# Revit family: Heater-QMark-Explosion_Proof_Convection_Heater_Gen2
name_source: partatom
category: Mechanical Equipment
units: mm (PartAtom-declared; Revit-internal decimal feet)

## family parameters
Classification = None
Cut with Voids When Loaded = No
Host = Face
OmniClass Number = 23.75.70.17.14
OmniClass Title = Convectors
Part Type = Normal
Room Calculation Point = No
Round Connector Dimension = Use Diameter
Shared = No

## types (191) — shared parameters
Default Elevation = 3' - 0"
Description = Electric explosion proof convection heater
Instruction Sheet Link = https://www.marleymep.com
Manufacturer = Marley® Engineered Products
Material = Paint - Berko - Tan
Number of Poles = 1
Product Documentation Link = https://www.marleymep.com
Product Name = Explosion - Proof Convection Heater Gen2
Product Page URL = https://www.marleymep.com
URL = https://www.marleymep.com
Version = 2020 - v1.0a

## per-type parameters (varying)
| type | Amps | Classification | Controls Only | Depth | Frequency | Height | Length | Phase | Power Factor | S1 - L 26in | S2 - L 26in | S2 - L 39in | S2 - L 67.5in | Shipping Weight | Thermostat only or w/controls | Total Heating Capacity | Unit Size | Voltage | Watts |
| Not a Type - Load Type Catalog | 0 A | Class I- Divisions 1 & 2- Groups B- C & D / Class I- Zones 1 & 2 Groups IIB + H2 / Ignition Temperature Code T2A- 536° F |  | 0' - 4 1/2" | 0 Hz | 0' - 6" | 2' - 2" | 1 | 0 | Yes | No | No | No |  |  | 0.0 Btu/h | 0 | 0 V | 0 W |
| QX-254-F0310052B | 4 A | Class I- Divisions 1 & 2- Groups B- C & D / Class I- Zones 1 & 2 Groups IIB + H2 / Ignition Temperature Code T2A- 536° F |  | 0' - 4 1/2" | 60 Hz | 0' - 6" | 2' - 2" | 1 | 1 | Yes | No | No | No | 13 lbs | 1024754 | 1706.0 Btu/h | 1 | 120 V | 500 W |
| QX-254-F0310052C | 2 A | Class I- Divisions 1 & 2- Groups B- C & D / Class I- Zones 1 & 2 Groups IIB + H2 / Ignition Temperature Code T2A- 536° F |  | 0' - 4 1/2" | 60 Hz | 0' - 6" | 2' - 2" | 1 | 1 | Yes | No | No | No | 13 lbs | 1024754 | 1706.0 Btu/h | 1 | 208 V | 500 W |
| QX-254-F0310052J | 2 A | Class I- Divisions 1 & 2- Groups B- C & D / Class I- Zones 1 & 2 Groups IIB + H2 / Ignition Temperature Code T2A- 536° F |  | 0' - 4 1/2" | 60 Hz | 0' - 6" | 2' - 2" | 1 | 1 | Yes | No | No | No | 13 lbs | 1024754 | 1706.0 Btu/h | 1 | 240 V | 500 W |
| QX-254-F0310052N | 2 A | Class I- Divisions 1 & 2- Groups B- C & D / Class I- Zones 1 & 2 Groups IIB + H2 / Ignition Temperature Code T2A- 536° F |  | 0' - 4 1/2" | 60 Hz | 0' - 6" | 2' - 2" | 1 | 1 | Yes | No | No | No | 13 lbs | 1024754 | 1706.0 Btu/h | 1 | 277 V | 500 W |
| QX-254-F0310102B | 8 A | Class I- Divisions 1 & 2- Groups B- C & D / Class I- Zones 1 & 2 Groups IIB + H2 / Ignition Temperature Code T2A- 536° F |  | 0' - 4 1/2" | 60 Hz | 0' - 6" | 2' - 2" | 1 | 1 | Yes | No | No | No | 13 lbs | 1024754 | 3412.0 Btu/h | 1 | 120 V | 1000 W |
| QX-254-F0310102C | 5 A | Class I- Divisions 1 & 2- Groups B- C & D / Class I- Zones 1 & 2 Groups IIB + H2 / Ignition Temperature Code T2A- 536° F |  | 0' - 4 1/2" | 60 Hz | 0' - 6" | 2' - 2" | 1 | 1 | Yes | No | No | No | 13 lbs | 1024754 | 3412.0 Btu/h | 1 | 208 V | 1000 W |
| QX-254-F0310102J | 4 A | Class I- Divisions 1 & 2- Groups B- C & D / Class I- Zones 1 & 2 Groups IIB + H2 / Ignition Temperature Code T2A- 536° F |  | 0' - 4 1/2" | 60 Hz | 0' - 6" | 2' - 2" | 1 | 1 | Yes | No | No | No | 13 lbs | 1024754 | 3412.0 Btu/h | 1 | 240 V | 1000 W |
| QX-254-F0310102N | 4 A | Class I- Divisions 1 & 2- Groups B- C & D / Class I- Zones 1 & 2 Groups IIB + H2 / Ignition Temperature Code T2A- 536° F |  | 0' - 4 1/2" | 60 Hz | 0' - 6" | 2' - 2" | 1 | 1 | Yes | No | No | No | 13 lbs | 1024754 | 3412.0 Btu/h | 1 | 277 V | 1000 W |
| QX-254-F0320182B | 15 A | Class I- Divisions 1 & 2- Groups B- C & D / Class I- Zones 1 & 2 Groups IIB + H2 / Ignition Temperature Code T2A- 536° F | Not Required | 0' - 8" | 60 Hz | 1' - 4" | 2' - 2" | 1 | 1 | No | Yes | No | No | 13 lbs | S2 | 6140.0 Btu/h | 2 | 120 V | 1800 W |
| QX-254-F0320182C | 9 A | Class I- Divisions 1 & 2- Groups B- C & D / Class I- Zones 1 & 2 Groups IIB + H2 / Ignition Temperature Code T2A- 536° F | Not Required | 0' - 8" | 60 Hz | 1' - 4" | 2' - 2" | 1 | 1 | No | Yes | No | No | 27 lbs | S2 | 6140.0 Btu/h | 2 | 208 V | 1800 W |
| QX-254-F0320182J | 8 A | Class I- Divisions 1 & 2- Groups B- C & D / Class I- Zones 1 & 2 Groups IIB + H2 / Ignition Temperature Code T2A- 536° F | Not Required | 0' - 8" | 60 Hz | 1' - 4" | 2' - 2" | 1 | 1 | No | Yes | No | No | 27 lbs | S2 | 6140.0 Btu/h | 2 | 240 V | 1800 W |
| QX-254-F0320182N | 7 A | Class I- Divisions 1 & 2- Groups B- C & D / Class I- Zones 1 & 2 Groups IIB + H2 / Ignition Temperature Code T2A- 536° F | Not Required | 0' - 8" | 60 Hz | 1' - 4" | 2' - 2" | 1 | 1 | No | Yes | No | No | 27 lbs | S2 | 6140.0 Btu/h | 2 | 277 V | 1800 W |
| QX-254-F0320182I | 5 A | Class I- Divisions 1 & 2- Groups B- C & D / Class I- Zones 1 & 2 Groups IIB + H2 / Ignition Temperature Code T2A- 536° F | B2 | 0' - 8" | 60 Hz | 1' - 4" | 2' - 2" | 1 | 1 | No | Yes | No | No | 27 lbs | B3 | 6140.0 Btu/h | 2 | 347 V | 1800 W |
| QX-254-F0320182U | 2 A | Class I- Divisions 1 & 2- Groups B- C & D / Class I- Zones 1 & 2 Groups IIB + H2 / Ignition Temperature Code T2A- 536° F | B2 | 0' - 8" | 60 Hz | 1' - 4" | 2' - 2" | 3 | 1 | No | Yes | No | No | 27 lbs | B3 | 6140.0 Btu/h | 2 | 480 V | 1800 W |
| QX-254-F0320182Z | 2 A | Class I- Divisions 1 & 2- Groups B- C & D / Class I- Zones 1 & 2 Groups IIB + H2 / Ignition Temperature Code T2A- 536° F | B2 | 0' - 8" | 60 Hz | 1' - 4" | 2' - 2" | 3 | 1 | No | Yes | No | No | 27 lbs | B3 | 6140.0 Btu/h | 2 | 600 V | 1800 W |
| QX-254-F0320252C | 12 A | Class I- Divisions 1 & 2- Groups B- C & D / Class I- Zones 1 & 2 Groups IIB + H2 / Ignition Temperature Code T2A- 536° F | Not Required | 0' - 8" | 60 Hz | 1' - 4" | 2' - 2" | 1 | 1 | No | Yes | No | No | 27 lbs | S2 | 8530.0 Btu/h | 2 | 208 V | 2500 W |
| QX-254-F0320252D | 7 A | Class I- Divisions 1 & 2- Groups B- C & D / Class I- Zones 1 & 2 Groups IIB + H2 / Ignition Temperature Code T2A- 536° F | B2 | 0' - 8" | 60 Hz | 1' - 4" | 2' - 2" | 3 | 1 | No | Yes | No | No | 27 lbs | B3 | 8530.0 Btu/h | 2 | 208 V | 2500 W |
| QX-254-F0320252J | 10 A | Class I- Divisions 1 & 2- Groups B- C & D / Class I- Zones 1 & 2 Groups IIB + H2 / Ignition Temperature Code T2A- 536° F | Not Required | 0' - 8" | 60 Hz | 1' - 4" | 2' - 2" | 1 | 1 | No | Yes | No | No | 27 lbs | S2 | 8530.0 Btu/h | 2 | 240 V | 2500 W |
| QX-254-F0320252N | 9 A | Class I- Divisions 1 & 2- Groups B- C & D / Class I- Zones 1 & 2 Groups IIB + H2 / Ignition Temperature Code T2A- 536° F | Not Required | 0' - 8" | 60 Hz | 1' - 4" | 2' - 2" | 1 | 1 | No | Yes | No | No | 27 lbs | S2 | 8530.0 Btu/h | 2 | 277 V | 2500 W |
| QX-254-F0320252I | 7 A | Class I- Divisions 1 & 2- Groups B- C & D / Class I- Zones 1 & 2 Groups IIB + H2 / Ignition Temperature Code T2A- 536° F | B2 | 0' - 8" | 60 Hz | 1' - 4" | 2' - 2" | 1 | 1 | No | Yes | No | No | 27 lbs | B3 | 8530.0 Btu/h | 2 | 347 V | 2500 W |
| QX-254-F0320252U | 3 A | Class I- Divisions 1 & 2- Groups B- C & D / Class I- Zones 1 & 2 Groups IIB + H2 / Ignition Temperature Code T2A- 536° F | B2 | 0' - 8" | 60 Hz | 1' - 4" | 2' - 2" | 3 | 1 | No | Yes | No | No | 27 lbs | B3 | 8530.0 Btu/h | 2 | 480 V | 2500 W |
| QX-254-F0320252Z | 2 A | Class I- Divisions 1 & 2- Groups B- C & D / Class I- Zones 1 & 2 Groups IIB + H2 / Ignition Temperature Code T2A- 536° F | B2 | 0' - 8" | 60 Hz | 1' - 4" | 2' - 2" | 3 | 1 | No | Yes | No | No | 27 lbs | B3 | 8530.0 Btu/h | 2 | 600 V | 2500 W |
| QX-254-F0330362C | 17 A | Class I- Divisions 1 & 2- Groups B- C & D / Class I- Zones 1 & 2 Groups IIB + H2 / Ignition Temperature Code T2A- 536° F | Not Required | 0' - 8" | 60 Hz | 1' - 4" | 3' - 3" | 1 | 1 | No | No | Yes | No | 36 lbs | S2 | 12283.0 Btu/h | 3 | 208 V | 3600 W |
| QX-254-F0330362D | 10 A | Class I- Divisions 1 & 2- Groups B- C & D / Class I- Zones 1 & 2 Groups IIB + H2 / Ignition Temperature Code T2A- 536° F | B2 | 0' - 8" | 60 Hz | 1' - 4" | 3' - 3" | 3 | 1 | No | No | Yes | No | 36 lbs | B3 | 12283.0 Btu/h | 3 | 208 V | 3600 W |
| QX-254-F0330362J | 15 A | Class I- Divisions 1 & 2- Groups B- C & D / Class I- Zones 1 & 2 Groups IIB + H2 / Ignition Temperature Code T2A- 536° F | Not Required | 0' - 8" | 60 Hz | 1' - 4" | 3' - 3" | 1 | 1 | No | No | Yes | No | 36 lbs | S2 | 12283.0 Btu/h | 3 | 240 V | 3600 W |
| QX-254-F0330362N | 13 A | Class I- Divisions 1 & 2- Groups B- C & D / Class I- Zones 1 & 2 Groups IIB + H2 / Ignition Temperature Code T2A- 536° F | Not Required | 0' - 8" | 60 Hz | 1' - 4" | 3' - 3" | 1 | 1 | No | No | Yes | No | 36 lbs | S2 | 12283.0 Btu/h | 3 | 277 V | 3600 W |
| QX-254-F0330362I | 10 A | Class I- Divisions 1 & 2- Groups B- C & D / Class I- Zones 1 & 2 Groups IIB + H2 / Ignition Temperature Code T2A- 536° F | B2 | 0' - 8" | 60 Hz | 1' - 4" | 3' - 3" | 1 | 1 | No | No | Yes | No | 36 lbs | B3 | 12283.0 Btu/h | 3 | 347 V | 3600 W |
| QX-254-F0330362U | 4 A | Class I- Divisions 1 & 2- Groups B- C & D / Class I- Zones 1 & 2 Groups IIB + H2 / Ignition Temperature Code T2A- 536° F | B2 | 0' - 8" | 60 Hz | 1' - 4" | 3' - 3" | 3 | 1 | No | No | Yes | No | 36 lbs | B3 | 12283.0 Btu/h | 3 | 480 V | 3600 W |
| QX-254-F0330362Z | 4 A | Class I- Divisions 1 & 2- Groups B- C & D / Class I- Zones 1 & 2 Groups IIB + H2 / Ignition Temperature Code T2A- 536° F | B2 | 0' - 8" | 60 Hz | 1' - 4" | 3' - 3" | 3 | 1 | No | No | Yes | No | 36 lbs | B3 | 12283.0 Btu/h | 3 | 600 V | 3600 W |
| QX-254-F0330442D | 12 A | Class I- Divisions 1 & 2- Groups B- C & D / Class I- Zones 1 & 2 Groups IIB + H2 / Ignition Temperature Code T2A- 536° F | B2 | 0' - 8" | 60 Hz | 1' - 4" | 3' - 3" | 3 | 1 | No | No | Yes | No | 36 lbs | B3 | 15013.0 Btu/h | 3 | 208 V | 4400 W |
| QX-254-F0330442J | 18 A | Class I- Divisions 1 & 2- Groups B- C & D / Class I- Zones 1 & 2 Groups IIB + H2 / Ignition Temperature Code T2A- 536° F | Not Required | 0' - 8" | 60 Hz | 1' - 4" | 3' - 3" | 1 | 1 | No | No | Yes | No | 36 lbs | S2 | 15013.0 Btu/h | 3 | 240 V | 4400 W |
| QX-254-F0330442N | 16 A | Class I- Divisions 1 & 2- Groups B- C & D / Class I- Zones 1 & 2 Groups IIB + H2 / Ignition Temperature Code T2A- 536° F | Not Required | 0' - 8" | 60 Hz | 1' - 4" | 3' - 3" | 1 | 1 | No | No | Yes | No | 36 lbs | S2 | 15013.0 Btu/h | 3 | 277 V | 4400 W |
| QX-254-F0330442I | 13 A | Class I- Divisions 1 & 2- Groups B- C & D / Class I- Zones 1 & 2 Groups IIB + H2 / Ignition Temperature Code T2A- 536° F | B2 | 0' - 8" | 60 Hz | 1' - 4" | 3' - 3" | 1 | 1 | No | No | Yes | No | 36 lbs | B3 | 15013.0 Btu/h | 3 | 347 V | 4400 W |
| QX-254-F0330442U | 5 A | Class I- Divisions 1 & 2- Groups B- C & D / Class I- Zones 1 & 2 Groups IIB + H2 / Ignition Temperature Code T2A- 536° F | B2 | 0' - 8" | 60 Hz | 1' - 4" | 3' - 3" | 3 | 1 | No | No | Yes | No | 36 lbs | B3 | 15013.0 Btu/h | 3 | 480 V | 4400 W |
| QX-254-F0330442Z | 4 A | Class I- Divisions 1 & 2- Groups B- C & D / Class I- Zones 1 & 2 Groups IIB + H2 / Ignition Temperature Code T2A- 536° F | B2 | 0' - 8" | 60 Hz | 1' - 4" | 3' - 3" | 3 | 1 | No | No | Yes | No | 36 lbs | B3 | 15013.0 Btu/h | 3 | 600 V | 4400 W |
| QX-254-F0340652D | 18 A | Class I- Divisions 1 & 2- Groups B- C & D / Class I- Zones 1 & 2 Groups IIB + H2 / Ignition Temperature Code T2A- 536° F | B2 | 0' - 8" | 60 Hz | 1' - 4" | 5' - 7 1/2" | 3 | 1 | No | No | No | Yes | 60 lbs | B3 | 22178.0 Btu/h | 4 | 208 V | 6500 W |
| QX-254-F0340652J | 27 A | Class I- Divisions 1 & 2- Groups B- C & D / Class I- Zones 1 & 2 Groups IIB + H2 / Ignition Temperature Code T2A- 536° F | B2 | 0' - 8" | 60 Hz | 1' - 4" | 5' - 7 1/2" | 3 | 1 | No | No | No | Yes | 60 lbs | B3 | 22178.0 Btu/h | 4 | 240 V | 6500 W |
| QX-254-F0340652N | 24 A | Class I- Divisions 1 & 2- Groups B- C & D / Class I- Zones 1 & 2 Groups IIB + H2 / Ignition Temperature Code T2A- 536° F | B2 | 0' - 8" | 60 Hz | 1' - 4" | 5' - 7 1/2" | 1 | 1 | No | No | No | Yes | 60 lbs | B3 | 22178.0 Btu/h | 4 | 277 V | 6500 W |
| QX-254-F0340652I | 19 A | Class I- Divisions 1 & 2- Groups B- C & D / Class I- Zones 1 & 2 Groups IIB + H2 / Ignition Temperature Code T2A- 536° F | B2 | 0' - 8" | 60 Hz | 1' - 4" | 5' - 7 1/2" | 1 | 1 | No | No | No | Yes | 60 lbs | B3 | 22178.0 Btu/h | 4 | 347 V | 6500 W |
| QX-254-F0340652U | 8 A | Class I- Divisions 1 & 2- Groups B- C & D / Class I- Zones 1 & 2 Groups IIB + H2 / Ignition Temperature Code T2A- 536° F | B2 | 0' - 8" | 60 Hz | 1' - 4" | 5' - 7 1/2" | 3 | 1 | No | No | No | Yes | 60 lbs | B3 | 22178.0 Btu/h | 4 | 480 V | 6500 W |
| QX-254-F0340652Z | 6 A | Class I- Divisions 1 & 2- Groups B- C & D / Class I- Zones 1 & 2 Groups IIB + H2 / Ignition Temperature Code T2A- 536° F | B2 | 0' - 8" | 60 Hz | 1' - 4" | 5' - 7 1/2" | 3 | 1 | No | No | No | Yes | 60 lbs | B3 | 22178.0 Btu/h | 4 | 600 V | 6500 W |
| QX-254-F0340752D | 21 A | Class I- Divisions 1 & 2- Groups B- C & D / Class I- Zones 1 & 2 Groups IIB + H2 / Ignition Temperature Code T2A- 536° F | B2 | 0' - 8" | 60 Hz | 1' - 4" | 5' - 7 1/2" | 3 | 1 | No | No | No | Yes | 60 lbs | B3 | 25590.0 Btu/h | 4 | 208 V | 7500 W |
| QX-254-F0340752J | 31 A | Class I- Divisions 1 & 2- Groups B- C & D / Class I- Zones 1 & 2 Groups IIB + H2 / Ignition Temperature Code T2A- 536° F | B2 | 0' - 8" | 60 Hz | 1' - 4" | 5' - 7 1/2" | 1 | 1 | No | No | No | Yes | 60 lbs | B3 | 25590.0 Btu/h | 4 | 240 V | 7500 W |
| QX-254-F0340752N | 27 A | Class I- Divisions 1 & 2- Groups B- C & D / Class I- Zones 1 & 2 Groups IIB + H2 / Ignition Temperature Code T2A- 536° F | B2 | 0' - 8" | 60 Hz | 1' - 4" | 5' - 7 1/2" | 1 | 1 | No | No | No | Yes | 60 lbs | B3 | 25590.0 Btu/h | 4 | 277 V | 7500 W |
| QX-254-F0340752I | 22 A | Class I- Divisions 1 & 2- Groups B- C & D / Class I- Zones 1 & 2 Groups IIB + H2 / Ignition Temperature Code T2A- 536° F | B2 | 0' - 8" | 60 Hz | 1' - 4" | 5' - 7 1/2" | 1 | 1 | No | No | No | Yes | 60 lbs | B3 | 25590.0 Btu/h | 4 | 347 V | 7500 W |
| QX-254-F0340752U | 9 A | Class I- Divisions 1 & 2- Groups B- C & D / Class I- Zones 1 & 2 Groups IIB + H2 / Ignition Temperature Code T2A- 536° F | B2 | 0' - 8" | 60 Hz | 1' - 4" | 5' - 7 1/2" | 3 | 1 | No | No | No | Yes | 60 lbs | B3 | 25590.0 Btu/h | 4 | 480 V | 7500 W |
| QX-254-F0340752Z | 7 A | Class I- Divisions 1 & 2- Groups B- C & D / Class I- Zones 1 & 2 Groups IIB + H2 / Ignition Temperature Code T2A- 536° F | B2 | 0' - 8" | 60 Hz | 1' - 4" | 5' - 7 1/2" | 3 | 1 | No | No | No | Yes | 60 lbs | B3 | 25590.0 Btu/h | 4 | 600 V | 7500 W |
| QX-254-F0340952D | 26 A | Class I- Divisions 1 & 2- Groups B- C & D / Class I- Zones 1 & 2 Groups IIB + H2 / Ignition Temperature Code T2A- 536° F | B2 | 0' - 8" | 60 Hz | 1' - 4" | 5' - 7 1/2" | 3 | 1 | No | No | No | Yes | 60 lbs | B3 | 32415.0 Btu/h | 4 | 208 V | 9500 W |
| QX-254-F0340952J | 40 A | Class I- Divisions 1 & 2- Groups B- C & D / Class I- Zones 1 & 2 Groups IIB + H2 / Ignition Temperature Code T2A- 536° F | B2 | 0' - 8" | 60 Hz | 1' - 4" | 5' - 7 1/2" | 1 | 1 | No | No | No | Yes | 60 lbs | B3 | 32415.0 Btu/h | 4 | 240 V | 9500 W |
| QX-254-F0340952N | 34 A | Class I- Divisions 1 & 2- Groups B- C & D / Class I- Zones 1 & 2 Groups IIB + H2 / Ignition Temperature Code T2A- 536° F | B2 | 0' - 8" | 60 Hz | 1' - 4" | 5' - 7 1/2" | 1 | 1 | No | No | No | Yes | 60 lbs | B3 | 32415.0 Btu/h | 4 | 277 V | 9500 W |
| QX-254-F0340952I | 27 A | Class I- Divisions 1 & 2- Groups B- C & D / Class I- Zones 1 & 2 Groups IIB + H2 / Ignition Temperature Code T2A- 536° F | B2 | 0' - 8" | 60 Hz | 1' - 4" | 5' - 7 1/2" | 1 | 1 | No | No | No | Yes | 60 lbs | B3 | 32415.0 Btu/h | 4 | 347 V | 9500 W |
| QX-254-F0340952U | 11 A | Class I- Divisions 1 & 2- Groups B- C & D / Class I- Zones 1 & 2 Groups IIB + H2 / Ignition Temperature Code T2A- 536° F | B2 | 0' - 8" | 60 Hz | 1' - 4" | 5' - 7 1/2" | 3 | 1 | No | No | No | Yes | 60 lbs | B3 | 32415.0 Btu/h | 4 | 480 V | 9500 W |
| QX-254-F0340952Z | 9 A | Class I- Divisions 1 & 2- Groups B- C & D / Class I- Zones 1 & 2 Groups IIB + H2 / Ignition Temperature Code T2A- 536° F | B2 | 0' - 8" | 60 Hz | 1' - 4" | 5' - 7 1/2" | 3 | 1 | No | No | No | Yes | 60 lbs | B3 | 32415.0 Btu/h | 4 | 600 V | 9500 W |
| QX-254-F0310053B | 4 A | Class I- Divisions 1 & 2- Groups C & D / Class I- Zones 1 & 2 Groups IIB / Ignition Temperature Code T2A- 536° F |  | 0' - 4 1/2" | 60 Hz | 0' - 6" | 2' - 2" | 1 | 1 | Yes | No | No | No | 13 lbs | 1007002 | 1706.0 Btu/h | 1 | 120 V | 500 W |
| QX-254-F0310053C | 2 A | Class I- Divisions 1 & 2- Groups C & D / Class I- Zones 1 & 2 Groups IIB / Ignition Temperature Code T2A- 536° F |  | 0' - 4 1/2" | 60 Hz | 0' - 6" | 2' - 2" | 1 | 1 | Yes | No | No | No | 13 lbs | 1007002 | 1706.0 Btu/h | 1 | 208 V | 500 W |
| QX-254-F0310053J | 2 A | Class I- Divisions 1 & 2- Groups C & D / Class I- Zones 1 & 2 Groups IIB / Ignition Temperature Code T2A- 536° F |  | 0' - 4 1/2" | 60 Hz | 0' - 6" | 2' - 2" | 1 | 1 | Yes | No | No | No | 13 lbs | 1007002 | 1706.0 Btu/h | 1 | 240 V | 500 W |
| QX-254-F0310053N | 2 A | Class I- Divisions 1 & 2- Groups C & D / Class I- Zones 1 & 2 Groups IIB / Ignition Temperature Code T2A- 536° F |  | 0' - 4 1/2" | 60 Hz | 0' - 6" | 2' - 2" | 1 | 1 | Yes | No | No | No | 13 lbs | 1007002 | 1706.0 Btu/h | 1 | 277 V | 500 W |
| QX-254-F0310103B | 8 A | Class I- Divisions 1 & 2- Groups C & D / Class I- Zones 1 & 2 Groups IIB / Ignition Temperature Code T2A- 536° F |  | 0' - 4 1/2" | 60 Hz | 0' - 6" | 2' - 2" | 1 | 1 | Yes | No | No | No | 13 lbs | 1007002 | 3412.0 Btu/h | 1 | 120 V | 1000 W |
| QX-254-F0310103C | 5 A | Class I- Divisions 1 & 2- Groups C & D / Class I- Zones 1 & 2 Groups IIB / Ignition Temperature Code T2A- 536° F |  | 0' - 4 1/2" | 60 Hz | 0' - 6" | 2' - 2" | 1 | 1 | Yes | No | No | No | 13 lbs | 1007002 | 3412.0 Btu/h | 1 | 208 V | 1000 W |
| QX-254-F0310103J | 4 A | Class I- Divisions 1 & 2- Groups C & D / Class I- Zones 1 & 2 Groups IIB / Ignition Temperature Code T2A- 536° F |  | 0' - 4 1/2" | 60 Hz | 0' - 6" | 2' - 2" | 1 | 1 | Yes | No | No | No | 13 lbs | 1007002 | 3412.0 Btu/h | 1 | 240 V | 1000 W |
| QX-254-F0310103N | 4 A | Class I- Divisions 1 & 2- Groups C & D / Class I- Zones 1 & 2 Groups IIB / Ignition Temperature Code T2A- 536° F |  | 0' - 4 1/2" | 60 Hz | 0' - 6" | 2' - 2" | 1 | 1 | Yes | No | No | No | 13 lbs | 1007002 | 3412.0 Btu/h | 1 | 277 V | 1000 W |
| QX-254-F0320183B | 15 A | Class I- Divisions 1 & 2- Groups C & D / Class I- Zones 1 & 2 Groups IIB / Ignition Temperature Code T2A- 536° F | Not Required | 0' - 8" | 60 Hz | 1' - 4" | 2' - 2" | 1 | 1 | No | Yes | No | No | 27 lbs | S1 | 6140.0 Btu/h | 2 | 120 V | 1800 W |
| QX-254-F0320183C | 9 A | Class I- Divisions 1 & 2- Groups C & D / Class I- Zones 1 & 2 Groups IIB / Ignition Temperature Code T2A- 536° F | Not Required | 0' - 8" | 60 Hz | 1' - 4" | 2' - 2" | 1 | 1 | No | Yes | No | No | 27 lbs | S1 | 6140.0 Btu/h | 2 | 208 V | 1800 W |
| QX-254-F0320183J | 8 A | Class I- Divisions 1 & 2- Groups C & D / Class I- Zones 1 & 2 Groups IIB / Ignition Temperature Code T2A- 536° F | Not Required | 0' - 8" | 60 Hz | 1' - 4" | 2' - 2" | 1 | 1 | No | Yes | No | No | 27 lbs | S1 | 6140.0 Btu/h | 2 | 240 V | 1800 W |
| QX-254-F0320183N | 7 A | Class I- Divisions 1 & 2- Groups C & D / Class I- Zones 1 & 2 Groups IIB / Ignition Temperature Code T2A- 536° F | Not Required | 0' - 8" | 60 Hz | 1' - 4" | 2' - 2" | 1 | 1 | No | Yes | No | No | 27 lbs | S1 | 6140.0 Btu/h | 2 | 277 V | 1800 W |
| QX-254-F0320183I | 5 A | Class I- Divisions 1 & 2- Groups C & D / Class I- Zones 1 & 2 Groups IIB / Ignition Temperature Code T2A- 536° F | B2 | 0' - 8" | 60 Hz | 1' - 4" | 2' - 2" | 1 | 1 | No | Yes | No | No | 27 lbs | B2S1 | 6140.0 Btu/h | 2 | 347 V | 1800 W |
| QX-254-F0320183U | 2 A | Class I- Divisions 1 & 2- Groups C & D / Class I- Zones 1 & 2 Groups IIB / Ignition Temperature Code T2A- 536° F | B2 | 0' - 8" | 60 Hz | 1' - 4" | 2' - 2" | 3 | 1 | No | Yes | No | No | 27 lbs | B2S1 | 6140.0 Btu/h | 2 | 480 V | 1800 W |
| QX-254-F0320183Z | 2 A | Class I- Divisions 1 & 2- Groups C & D / Class I- Zones 1 & 2 Groups IIB / Ignition Temperature Code T2A- 536° F | B2 | 0' - 8" | 60 Hz | 1' - 4" | 2' - 2" | 3 | 1 | No | Yes | No | No | 27 lbs | B2S1 | 6140.0 Btu/h | 2 | 600 V | 1800 W |
| QX-254-F0320253C | 12 A | Class I- Divisions 1 & 2- Groups C & D / Class I- Zones 1 & 2 Groups IIB / Ignition Temperature Code T2A- 536° F | Not Required | 0' - 8" | 60 Hz | 1' - 4" | 2' - 2" | 1 | 1 | No | Yes | No | No | 27 lbs | S1 | 8530.0 Btu/h | 2 | 208 V | 2500 W |
| QX-254-F0320253D | 7 A | Class I- Divisions 1 & 2- Groups C & D / Class I- Zones 1 & 2 Groups IIB / Ignition Temperature Code T2A- 536° F | B2 | 0' - 8" | 60 Hz | 1' - 4" | 2' - 2" | 3 | 1 | No | Yes | No | No | 27 lbs | B2S1 | 8530.0 Btu/h | 2 | 208 V | 2500 W |
| QX-254-F0320253J | 10 A | Class I- Divisions 1 & 2- Groups C & D / Class I- Zones 1 & 2 Groups IIB / Ignition Temperature Code T2A- 536° F | Not Required | 0' - 8" | 60 Hz | 1' - 4" | 2' - 2" | 1 | 1 | No | Yes | No | No | 27 lbs | S1 | 8530.0 Btu/h | 2 | 240 V | 2500 W |
| QX-254-F0320253N | 9 A | Class I- Divisions 1 & 2- Groups C & D / Class I- Zones 1 & 2 Groups IIB / Ignition Temperature Code T2A- 536° F | Not Required | 0' - 8" | 60 Hz | 1' - 4" | 2' - 2" | 1 | 1 | No | Yes | No | No | 27 lbs | S1 | 8530.0 Btu/h | 2 | 277 V | 2500 W |
| QX-254-F0320253I | 7 A | Class I- Divisions 1 & 2- Groups C & D / Class I- Zones 1 & 2 Groups IIB / Ignition Temperature Code T2A- 536° F | B2 | 0' - 8" | 60 Hz | 1' - 4" | 2' - 2" | 1 | 1 | No | Yes | No | No | 27 lbs | B2S1 | 8530.0 Btu/h | 2 | 347 V | 2500 W |
| QX-254-F0320253U | 3 A | Class I- Divisions 1 & 2- Groups C & D / Class I- Zones 1 & 2 Groups IIB / Ignition Temperature Code T2A- 536° F | B2 | 0' - 8" | 60 Hz | 1' - 4" | 2' - 2" | 3 | 1 | No | Yes | No | No | 27 lbs | B2S1 | 8530.0 Btu/h | 2 | 480 V | 2500 W |
| QX-254-F0320253Z | 2 A | Class I- Divisions 1 & 2- Groups C & D / Class I- Zones 1 & 2 Groups IIB / Ignition Temperature Code T2A- 536° F | B2 | 0' - 8" | 60 Hz | 1' - 4" | 2' - 2" | 3 | 1 | No | Yes | No | No | 27 lbs | B2S1 | 8530.0 Btu/h | 2 | 600 V | 2500 W |
| QX-254-F0330363C | 17 A | Class I- Divisions 1 & 2- Groups C & D / Class I- Zones 1 & 2 Groups IIB / Ignition Temperature Code T2A- 536° F | Not Required | 0' - 8" | 60 Hz | 1' - 4" | 3' - 3" | 1 | 1 | No | No | Yes | No | 36 lbs | S1 | 12283.0 Btu/h | 3 | 208 V | 3600 W |
| QX-254-F0330363D | 10 A | Class I- Divisions 1 & 2- Groups C & D / Class I- Zones 1 & 2 Groups IIB / Ignition Temperature Code T2A- 536° F | B2 | 0' - 8" | 60 Hz | 1' - 4" | 3' - 3" | 3 | 1 | No | No | Yes | No | 36 lbs | B2S1 | 12283.0 Btu/h | 3 | 208 V | 3600 W |
| QX-254-F0330363J | 15 A | Class I- Divisions 1 & 2- Groups C & D / Class I- Zones 1 & 2 Groups IIB / Ignition Temperature Code T2A- 536° F | Not Required | 0' - 8" | 60 Hz | 1' - 4" | 3' - 3" | 1 | 1 | No | No | Yes | No | 36 lbs | S1 | 12283.0 Btu/h | 3 | 240 V | 3600 W |
| QX-254-F0330363N | 13 A | Class I- Divisions 1 & 2- Groups C & D / Class I- Zones 1 & 2 Groups IIB / Ignition Temperature Code T2A- 536° F | Not Required | 0' - 8" | 60 Hz | 1' - 4" | 3' - 3" | 1 | 1 | No | No | Yes | No | 36 lbs | S1 | 12283.0 Btu/h | 3 | 277 V | 3600 W |
| QX-254-F0330363I | 10 A | Class I- Divisions 1 & 2- Groups C & D / Class I- Zones 1 & 2 Groups IIB / Ignition Temperature Code T2A- 536° F | B3 | 0' - 8" | 60 Hz | 1' - 4" | 3' - 3" | 1 | 1 | No | No | Yes | No | 36 lbs | B3S1 | 12283.0 Btu/h | 3 | 347 V | 3600 W |
| QX-254-F0330363U | 4 A | Class I- Divisions 1 & 2- Groups C & D / Class I- Zones 1 & 2 Groups IIB / Ignition Temperature Code T2A- 536° F | B2 | 0' - 8" | 60 Hz | 1' - 4" | 3' - 3" | 3 | 1 | No | No | Yes | No | 36 lbs | B2S1 | 12283.0 Btu/h | 3 | 480 V | 3600 W |
| QX-254-F0330363Z | 4 A | Class I- Divisions 1 & 2- Groups C & D / Class I- Zones 1 & 2 Groups IIB / Ignition Temperature Code T2A- 536° F | B2 | 0' - 8" | 60 Hz | 1' - 4" | 3' - 3" | 3 | 1 | No | No | Yes | No | 36 lbs | B2S1 | 12283.0 Btu/h | 3 | 600 V | 3600 W |
| QX-254-F0330443D | 12 A | Class I- Divisions 1 & 2- Groups C & D / Class I- Zones 1 & 2 Groups IIB / Ignition Temperature Code T2A- 536° F | B2 | 0' - 8" | 60 Hz | 1' - 4" | 3' - 3" | 3 | 1 | No | No | Yes | No | 36 lbs | B2S1 | 15013.0 Btu/h | 3 | 208 V | 4400 W |
| QX-254-F0330443J | 18 A | Class I- Divisions 1 & 2- Groups C & D / Class I- Zones 1 & 2 Groups IIB / Ignition Temperature Code T2A- 536° F | Not Required | 0' - 8" | 60 Hz | 1' - 4" | 3' - 3" | 1 | 1 | No | No | Yes | No | 36 lbs | S1 | 15013.0 Btu/h | 3 | 240 V | 4400 W |
| QX-254-F0330443N | 16 A | Class I- Divisions 1 & 2- Groups C & D / Class I- Zones 1 & 2 Groups IIB / Ignition Temperature Code T2A- 536° F | Not Required | 0' - 8" | 60 Hz | 1' - 4" | 3' - 3" | 1 | 1 | No | No | Yes | No | 36 lbs | S1 | 15013.0 Btu/h | 3 | 277 V | 4400 W |
| QX-254-F0330443I | 13 A | Class I- Divisions 1 & 2- Groups C & D / Class I- Zones 1 & 2 Groups IIB / Ignition Temperature Code T2A- 536° F | B2 | 0' - 8" | 60 Hz | 1' - 4" | 3' - 3" | 1 | 1 | No | No | Yes | No | 36 lbs | B3S1 | 15013.0 Btu/h | 3 | 347 V | 4400 W |
| QX-254-F0330443U | 5 A | Class I- Divisions 1 & 2- Groups C & D / Class I- Zones 1 & 2 Groups IIB / Ignition Temperature Code T2A- 536° F | B2 | 0' - 8" | 60 Hz | 1' - 4" | 3' - 3" | 3 | 1 | No | No | Yes | No | 36 lbs | B2S1 | 15013.0 Btu/h | 3 | 480 V | 4400 W |
| QX-254-F0330443Z | 4 A | Class I- Divisions 1 & 2- Groups C & D / Class I- Zones 1 & 2 Groups IIB / Ignition Temperature Code T2A- 536° F | B2 | 0' - 8" | 60 Hz | 1' - 4" | 3' - 3" | 3 | 1 | No | No | Yes | No | 36 lbs | B2S1 | 15013.0 Btu/h | 3 | 600 V | 4400 W |
| QX-254-F0340653D | 18 A | Class I- Divisions 1 & 2- Groups C & D / Class I- Zones 1 & 2 Groups IIB / Ignition Temperature Code T2A- 536° F | B2 | 0' - 8" | 60 Hz | 1' - 4" | 5' - 7 1/2" | 3 | 1 | No | No | No | Yes | 60 lbs | B2S1 | 22178.0 Btu/h | 4 | 208 V | 6500 W |
| QX-254-F0340653J | 27 A | Class I- Divisions 1 & 2- Groups C & D / Class I- Zones 1 & 2 Groups IIB / Ignition Temperature Code T2A- 536° F | B2 | 0' - 8" | 60 Hz | 1' - 4" | 5' - 7 1/2" | 1 | 1 | No | No | No | Yes | 60 lbs | B2S1 | 22178.0 Btu/h | 4 | 240 V | 6500 W |
| QX-254-F0340653N | 24 A | Class I- Divisions 1 & 2- Groups C & D / Class I- Zones 1 & 2 Groups IIB / Ignition Temperature Code T2A- 536° F | B2 | 0' - 8" | 60 Hz | 1' - 4" | 5' - 7 1/2" | 1 | 1 | No | No | No | Yes | 60 lbs | B2S1 | 22178.0 Btu/h | 4 | 277 V | 6500 W |
| QX-254-F0340653I | 19 A | Class I- Divisions 1 & 2- Groups C & D / Class I- Zones 1 & 2 Groups IIB / Ignition Temperature Code T2A- 536° F | B2 | 0' - 8" | 60 Hz | 1' - 4" | 5' - 7 1/2" | 1 | 1 | No | No | No | Yes | 60 lbs | B2S1 | 22178.0 Btu/h | 4 | 347 V | 6500 W |
| QX-254-F0340653U | 8 A | Class I- Divisions 1 & 2- Groups C & D / Class I- Zones 1 & 2 Groups IIB / Ignition Temperature Code T2A- 536° F | B2 | 0' - 8" | 60 Hz | 1' - 4" | 5' - 7 1/2" | 3 | 1 | No | No | No | Yes | 60 lbs | B2S1 | 22178.0 Btu/h | 4 | 480 V | 6500 W |
| QX-254-F0340653Z | 6 A | Class I- Divisions 1 & 2- Groups C & D / Class I- Zones 1 & 2 Groups IIB / Ignition Temperature Code T2A- 536° F | B2 | 0' - 8" | 60 Hz | 1' - 4" | 5' - 7 1/2" | 3 | 1 | No | No | No | Yes | 60 lbs | B2S1 | 22178.0 Btu/h | 4 | 600 V | 6500 W |
| QX-254-F0340753D | 21 A | Class I- Divisions 1 & 2- Groups C & D / Class I- Zones 1 & 2 Groups IIB / Ignition Temperature Code T2A- 536° F | B2 | 0' - 8" | 60 Hz | 1' - 4" | 5' - 7 1/2" | 3 | 1 | No | No | No | Yes | 60 lbs | B2S1 | 25590.0 Btu/h | 4 | 208 V | 7500 W |
| QX-254-F0340753J | 31 A | Class I- Divisions 1 & 2- Groups C & D / Class I- Zones 1 & 2 Groups IIB / Ignition Temperature Code T2A- 536° F | B2 | 0' - 8" | 60 Hz | 1' - 4" | 5' - 7 1/2" | 1 | 1 | No | No | No | Yes | 60 lbs | B2S1 | 25590.0 Btu/h | 4 | 240 V | 7500 W |
| QX-254-F0340753N | 27 A | Class I- Divisions 1 & 2- Groups C & D / Class I- Zones 1 & 2 Groups IIB / Ignition Temperature Code T2A- 536° F | B2 | 0' - 8" | 60 Hz | 1' - 4" | 5' - 7 1/2" | 1 | 1 | No | No | No | Yes | 60 lbs | B2S1 | 25590.0 Btu/h | 4 | 277 V | 7500 W |
| QX-254-F0340753I | 22 A | Class I- Divisions 1 & 2- Groups C & D / Class I- Zones 1 & 2 Groups IIB / Ignition Temperature Code T2A- 536° F | B2 | 0' - 8" | 60 Hz | 1' - 4" | 5' - 7 1/2" | 1 | 1 | No | No | No | Yes | 60 lbs | B2S1 | 25590.0 Btu/h | 4 | 347 V | 7500 W |
| QX-254-F0340753U | 9 A | Class I- Divisions 1 & 2- Groups C & D / Class I- Zones 1 & 2 Groups IIB / Ignition Temperature Code T2A- 536° F | B2 | 0' - 8" | 60 Hz | 1' - 4" | 5' - 7 1/2" | 3 | 1 | No | No | No | Yes | 60 lbs | B2S1 | 25590.0 Btu/h | 4 | 480 V | 7500 W |
| QX-254-F0340753Z | 7 A | Class I- Divisions 1 & 2- Groups C & D / Class I- Zones 1 & 2 Groups IIB / Ignition Temperature Code T2A- 536° F | B2 | 0' - 8" | 60 Hz | 1' - 4" | 5' - 7 1/2" | 3 | 1 | No | No | No | Yes | 60 lbs | B2S1 | 25590.0 Btu/h | 4 | 600 V | 7500 W |
| QX-254-F0340953D | 26 A | Class I- Divisions 1 & 2- Groups C & D / Class I- Zones 1 & 2 Groups IIB / Ignition Temperature Code T2A- 536° F | B2 | 0' - 8" | 60 Hz | 1' - 4" | 5' - 7 1/2" | 3 | 1 | No | No | No | Yes | 60 lbs | B2S1 | 32415.0 Btu/h | 4 | 208 V | 9500 W |
| QX-254-F0340953J | 40 A | Class I- Divisions 1 & 2- Groups C & D / Class I- Zones 1 & 2 Groups IIB / Ignition Temperature Code T2A- 536° F | B2 | 0' - 8" | 60 Hz | 1' - 4" | 5' - 7 1/2" | 1 | 1 | No | No | No | Yes | 60 lbs | B2S1 | 32415.0 Btu/h | 4 | 240 V | 9500 W |
| QX-254-F0340953N | 34 A | Class I- Divisions 1 & 2- Groups C & D / Class I- Zones 1 & 2 Groups IIB / Ignition Temperature Code T2A- 536° F | B2 | 0' - 8" | 60 Hz | 1' - 4" | 5' - 7 1/2" | 1 | 1 | No | No | No | Yes | 60 lbs | B2S1 | 32415.0 Btu/h | 4 | 277 V | 9500 W |
| QX-254-F0340953I | 27 A | Class I- Divisions 1 & 2- Groups C & D / Class I- Zones 1 & 2 Groups IIB / Ignition Temperature Code T2A- 536° F | B2 | 0' - 8" | 60 Hz | 1' - 4" | 5' - 7 1/2" | 1 | 1 | No | No | No | Yes | 60 lbs | B2S1 | 32415.0 Btu/h | 4 | 347 V | 9500 W |
| QX-254-F0340953U | 11 A | Class I- Divisions 1 & 2- Groups C & D / Class I- Zones 1 & 2 Groups IIB / Ignition Temperature Code T2A- 536° F | B2 | 0' - 8" | 60 Hz | 1' - 4" | 5' - 7 1/2" | 3 | 1 | No | No | No | Yes | 60 lbs | B2S1 | 32415.0 Btu/h | 4 | 480 V | 9500 W |
| QX-254-F0340953Z | 9 A | Class I- Divisions 1 & 2- Groups C & D / Class I- Zones 1 & 2 Groups IIB / Ignition Temperature Code T2A- 536° F | B2 | 0' - 8" | 60 Hz | 1' - 4" | 5' - 7 1/2" | 3 | 1 | No | No | No | Yes | 60 lbs | B2S1 | 32415.0 Btu/h | 4 | 600 V | 9500 W |
| QX-254-F0610052B | 4 A | Class I- Divisions 1 & 2- Groups B- C & D / Class I- Zones 1 & 2 Groups IIB + H2 / Ignition Temperature Code T3A- 356° F |  | 0' - 4 1/2" | 60 Hz | 0' - 6" | 2' - 2" | 1 | 1 | Yes | No | No | No | 13 lbs | 1024754 | 1706.0 Btu/h | 1 | 120 V | 500 W |
| QX-254-F0610052C | 2 A | Class I- Divisions 1 & 2- Groups B- C & D / Class I- Zones 1 & 2 Groups IIB + H2 / Ignition Temperature Code T3A- 356° F |  | 0' - 4 1/2" | 60 Hz | 0' - 6" | 2' - 2" | 1 | 1 | Yes | No | No | No | 13 lbs | 1024754 | 1706.0 Btu/h | 1 | 208 V | 500 W |
| QX-254-F0610052J | 2 A | Class I- Divisions 1 & 2- Groups B- C & D / Class I- Zones 1 & 2 Groups IIB + H2 / Ignition Temperature Code T3A- 356° F |  | 0' - 4 1/2" | 60 Hz | 0' - 6" | 2' - 2" | 1 | 1 | Yes | No | No | No | 13 lbs | 1024754 | 1706.0 Btu/h | 1 | 240 V | 500 W |
| QX-254-F0610052N | 2 A | Class I- Divisions 1 & 2- Groups B- C & D / Class I- Zones 1 & 2 Groups IIB + H2 / Ignition Temperature Code T3A- 356° F |  | 0' - 4 1/2" | 60 Hz | 0' - 6" | 2' - 2" | 1 | 1 | Yes | No | No | No | 13 lbs | 1024754 | 1706.0 Btu/h | 1 | 277 V | 500 W |
| QX-254-F0620142B | 12 A | Class I- Divisions 1 & 2- Groups B- C & D / Class I- Zones 1 & 2 Groups IIB + H2 / Ignition Temperature Code T3A- 356° F | Not Required | 0' - 8" | 60 Hz | 1' - 4" | 2' - 2" | 1 | 1 | No | Yes | No | No | 27 lbs | S2 | 4776.0 Btu/h | 2 | 120 V | 1400 W |
| QX-254-F0620142C | 7 A | Class I- Divisions 1 & 2- Groups B- C & D / Class I- Zones 1 & 2 Groups IIB + H2 / Ignition Temperature Code T3A- 356° F | Not Required | 0' - 8" | 60 Hz | 1' - 4" | 2' - 2" | 1 | 1 | No | Yes | No | No | 27 lbs | S2 | 4776.0 Btu/h | 2 | 208 V | 1400 W |
| QX-254-F0620142J | 6 A | Class I- Divisions 1 & 2- Groups B- C & D / Class I- Zones 1 & 2 Groups IIB + H2 / Ignition Temperature Code T3A- 356° F | Not Required | 0' - 8" | 60 Hz | 1' - 4" | 2' - 2" | 1 | 1 | No | Yes | No | No | 27 lbs | S2 | 4776.0 Btu/h | 2 | 240 V | 1400 W |
| QX-254-F0620142N | 5 A | Class I- Divisions 1 & 2- Groups B- C & D / Class I- Zones 1 & 2 Groups IIB + H2 / Ignition Temperature Code T3A- 356° F | Not Required | 0' - 8" | 60 Hz | 1' - 4" | 2' - 2" | 1 | 1 | No | Yes | No | No | 27 lbs | S2 | 4776.0 Btu/h | 2 | 277 V | 1400 W |
| QX-254-F0620142I | 4 A | Class I- Divisions 1 & 2- Groups B- C & D / Class I- Zones 1 & 2 Groups IIB + H2 / Ignition Temperature Code T3A- 356° F | B2 | 0' - 8" | 60 Hz | 1' - 4" | 2' - 2" | 1 | 1 | No | Yes | No | No | 27 lbs | B3 | 4776.0 Btu/h | 2 | 347 V | 1400 W |
| QX-254-F0630232B | 19 A | Class I- Divisions 1 & 2- Groups B- C & D / Class I- Zones 1 & 2 Groups IIB + H2 / Ignition Temperature Code T3A- 356° F | Not Required | 0' - 8" | 60 Hz | 1' - 4" | 3' - 3" | 1 | 1 | No | No | Yes | No | 36 lbs | S2 | 7847.0 Btu/h | 3 | 120 V | 2300 W |
| QX-254-F0630232C | 11 A | Class I- Divisions 1 & 2- Groups B- C & D / Class I- Zones 1 & 2 Groups IIB + H2 / Ignition Temperature Code T3A- 356° F | Not Required | 0' - 8" | 60 Hz | 1' - 4" | 3' - 3" | 1 | 1 | No | No | Yes | No | 36 lbs | S2 | 7847.0 Btu/h | 3 | 208 V | 2300 W |
| QX-254-F0630232D | 6 A | Class I- Divisions 1 & 2- Groups B- C & D / Class I- Zones 1 & 2 Groups IIB + H2 / Ignition Temperature Code T3A- 356° F | B2 | 0' - 8" | 60 Hz | 1' - 4" | 3' - 3" | 3 | 1 | No | No | Yes | No | 36 lbs | B3 | 7847.0 Btu/h | 3 | 208 V | 2300 W |
| QX-254-F0630232J | 10 A | Class I- Divisions 1 & 2- Groups B- C & D / Class I- Zones 1 & 2 Groups IIB + H2 / Ignition Temperature Code T3A- 356° F | Not Required | 0' - 8" | 60 Hz | 1' - 4" | 3' - 3" | 1 | 1 | No | No | Yes | No | 36 lbs | S2 | 7847.0 Btu/h | 3 | 240 V | 2300 W |
| QX-254-F0630232N | 8 A | Class I- Divisions 1 & 2- Groups B- C & D / Class I- Zones 1 & 2 Groups IIB + H2 / Ignition Temperature Code T3A- 356° F | Not Required | 0' - 8" | 60 Hz | 1' - 4" | 3' - 3" | 1 | 1 | No | No | Yes | No | 36 lbs | S2 | 7847.0 Btu/h | 3 | 277 V | 2300 W |
| QX-254-F0630232I | 7 A | Class I- Divisions 1 & 2- Groups B- C & D / Class I- Zones 1 & 2 Groups IIB + H2 / Ignition Temperature Code T3A- 356° F | B2 | 0' - 8" | 60 Hz | 1' - 4" | 3' - 3" | 1 | 1 | No | No | Yes | No | 36 lbs | B3 | 7847.0 Btu/h | 3 | 347 V | 2300 W |
| QX-254-F0630232U | 3 A | Class I- Divisions 1 & 2- Groups B- C & D / Class I- Zones 1 & 2 Groups IIB + H2 / Ignition Temperature Code T3A- 356° F | B2 | 0' - 8" | 60 Hz | 1' - 4" | 3' - 3" | 3 | 1 | No | No | Yes | No | 36 lbs | B3 | 7847.0 Btu/h | 3 | 480 V | 2300 W |
| QX-254-F0630232Z | 2 A | Class I- Divisions 1 & 2- Groups B- C & D / Class I- Zones 1 & 2 Groups IIB + H2 / Ignition Temperature Code T3A- 356° F | B2 | 0' - 8" | 60 Hz | 1' - 4" | 3' - 3" | 3 | 1 | No | No | Yes | No | 36 lbs | B3 | 7847.0 Btu/h | 3 | 600 V | 2300 W |
| QX-254-F0640322C | 15 A | Class I- Divisions 1 & 2- Groups B- C & D / Class I- Zones 1 & 2 Groups IIB + H2 / Ignition Temperature Code T3A- 356° F | Not Required | 0' - 8" | 60 Hz | 1' - 4" | 5' - 7 1/2" | 1 | 1 | No | No | No | Yes | 60 lbs | S2 | 10918.0 Btu/h | 4 | 208 V | 3200 W |
| QX-254-F0640322D | 9 A | Class I- Divisions 1 & 2- Groups B- C & D / Class I- Zones 1 & 2 Groups IIB + H2 / Ignition Temperature Code T3A- 356° F | B2 | 0' - 8" | 60 Hz | 1' - 4" | 5' - 7 1/2" | 3 | 1 | No | No | No | Yes | 60 lbs | B3 | 10918.0 Btu/h | 4 | 208 V | 3200 W |
| QX-254-F0640322J | 13 A | Class I- Divisions 1 & 2- Groups B- C & D / Class I- Zones 1 & 2 Groups IIB + H2 / Ignition Temperature Code T3A- 356° F | Not Required | 0' - 8" | 60 Hz | 1' - 4" | 5' - 7 1/2" | 1 | 1 | No | No | No | Yes | 60 lbs | S2 | 10918.0 Btu/h | 4 | 240 V | 3200 W |
| QX-254-F0640322N | 12 A | Class I- Divisions 1 & 2- Groups B- C & D / Class I- Zones 1 & 2 Groups IIB + H2 / Ignition Temperature Code T3A- 356° F | Not Required | 0' - 8" | 60 Hz | 1' - 4" | 5' - 7 1/2" | 1 | 1 | No | No | No | Yes | 60 lbs | S2 | 10918.0 Btu/h | 4 | 277 V | 3200 W |
| QX-254-F0640322I | 9 A | Class I- Divisions 1 & 2- Groups B- C & D / Class I- Zones 1 & 2 Groups IIB + H2 / Ignition Temperature Code T3A- 356° F | B2 | 0' - 8" | 60 Hz | 1' - 4" | 5' - 7 1/2" | 1 | 1 | No | No | No | Yes | 60 lbs | B3 | 10918.0 Btu/h | 4 | 347 V | 3200 W |
| QX-254-F0640322U | 4 A | Class I- Divisions 1 & 2- Groups B- C & D / Class I- Zones 1 & 2 Groups IIB + H2 / Ignition Temperature Code T3A- 356° F | B2 | 0' - 8" | 60 Hz | 1' - 4" | 5' - 7 1/2" | 3 | 1 | No | No | No | Yes | 60 lbs | B3 | 10918.0 Btu/h | 4 | 480 V | 3200 W |
| QX-254-F0640322Z | 3 A | Class I- Divisions 1 & 2- Groups B- C & D / Class I- Zones 1 & 2 Groups IIB + H2 / Ignition Temperature Code T3A- 356° F | B2 | 0' - 8" | 60 Hz | 1' - 4" | 5' - 7 1/2" | 3 | 1 | No | No | No | Yes | 60 lbs | B3 | 10918.0 Btu/h | 4 | 600 V | 3200 W |
| QX-254-F0640502D | 14 A | Class I- Divisions 1 & 2- Groups B- C & D / Class I- Zones 1 & 2 Groups IIB + H2 / Ignition Temperature Code T3A- 356° F | B2 | 0' - 8" | 60 Hz | 1' - 4" | 5' - 7 1/2" | 3 | 1 | No | No | No | Yes | 60 lbs | B3 | 17060.0 Btu/h | 4 | 208 V | 5000 W |
| QX-254-F0640502J | 21 A | Class I- Divisions 1 & 2- Groups B- C & D / Class I- Zones 1 & 2 Groups IIB + H2 / Ignition Temperature Code T3A- 356° F | Not Required | 0' - 8" | 60 Hz | 1' - 4" | 5' - 7 1/2" | 1 | 1 | No | No | No | Yes | 60 lbs | S2 | 17060.0 Btu/h | 4 | 240 V | 5000 W |
| QX-254-F0640502N | 18 A | Class I- Divisions 1 & 2- Groups B- C & D / Class I- Zones 1 & 2 Groups IIB + H2 / Ignition Temperature Code T3A- 356° F | Not Required | 0' - 8" | 60 Hz | 1' - 4" | 5' - 7 1/2" | 1 | 1 | No | No | No | Yes | 60 lbs | S2 | 17060.0 Btu/h | 4 | 277 V | 5000 W |
| QX-254-F0640502I | 14 A | Class I- Divisions 1 & 2- Groups B- C & D / Class I- Zones 1 & 2 Groups IIB + H2 / Ignition Temperature Code T3A- 356° F | B2 | 0' - 8" | 60 Hz | 1' - 4" | 5' - 7 1/2" | 1 | 1 | No | No | No | Yes | 60 lbs | B3 | 17060.0 Btu/h | 4 | 347 V | 5000 W |
| QX-254-F0640502U | 6 A | Class I- Divisions 1 & 2- Groups B- C & D / Class I- Zones 1 & 2 Groups IIB + H2 / Ignition Temperature Code T3A- 356° F | B2 | 0' - 8" | 60 Hz | 1' - 4" | 5' - 7 1/2" | 3 | 1 | No | No | No | Yes | 60 lbs | B3 | 17060.0 Btu/h | 4 | 480 V | 5000 W |
| QX-254-F0640502Z | 5 A | Class I- Divisions 1 & 2- Groups B- C & D / Class I- Zones 1 & 2 Groups IIB + H2 / Ignition Temperature Code T3A- 356° F | B2 | 0' - 8" | 60 Hz | 1' - 4" | 5' - 7 1/2" | 3 | 1 | No | No | No | Yes | 60 lbs | B3 | 17060.0 Btu/h | 4 | 600 V | 5000 W |
| QX-254-F0610053B | 4 A | Class I- Divisions 1 & 2- Groups C & D / Class I- Zones 1 & 2 Groups IIB / Ignition Temperature Code T3A- 356° F |  | 0' - 4 1/2" | 60 Hz | 0' - 6" | 2' - 2" | 1 | 1 | Yes | No | No | No | 13 lbs | 1007002 | 1706.0 Btu/h | 1 | 120 V | 500 W |
| QX-254-F0610053C | 2 A | Class I- Divisions 1 & 2- Groups C & D / Class I- Zones 1 & 2 Groups IIB / Ignition Temperature Code T3A- 356° F |  | 0' - 4 1/2" | 60 Hz | 0' - 6" | 2' - 2" | 1 | 1 | Yes | No | No | No | 13 lbs | 1007002 | 1706.0 Btu/h | 1 | 208 V | 500 W |
| QX-254-F0610053J | 2 A | Class I- Divisions 1 & 2- Groups C & D / Class I- Zones 1 & 2 Groups IIB / Ignition Temperature Code T3A- 356° F |  | 0' - 4 1/2" | 60 Hz | 0' - 6" | 2' - 2" | 1 | 1 | Yes | No | No | No | 13 lbs | 1007002 | 1706.0 Btu/h | 1 | 240 V | 500 W |
| QX-254-F0610053N | 2 A | Class I- Divisions 1 & 2- Groups C & D / Class I- Zones 1 & 2 Groups IIB / Ignition Temperature Code T3A- 356° F |  | 0' - 4 1/2" | 60 Hz | 0' - 6" | 2' - 2" | 1 | 1 | Yes | No | No | No | 13 lbs | 1007002 | 1706.0 Btu/h | 1 | 277 V | 500 W |
| QX-254-F0620143B | 12 A | Class I- Divisions 1 & 2- Groups C & D / Class I- Zones 1 & 2 Groups IIB / Ignition Temperature Code T3A- 356° F | Not Required | 0' - 8" | 60 Hz | 1' - 4" | 2' - 2" | 1 | 1 | No | Yes | No | No | 27 lbs | S1 | 4776.0 Btu/h | 2 | 120 V | 1400 W |
| QX-254-F0620143C | 7 A | Class I- Divisions 1 & 2- Groups C & D / Class I- Zones 1 & 2 Groups IIB / Ignition Temperature Code T3A- 356° F | Not Required | 0' - 8" | 60 Hz | 1' - 4" | 2' - 2" | 1 | 1 | No | Yes | No | No | 27 lbs | S1 | 4776.0 Btu/h | 2 | 208 V | 1400 W |
| QX-254-F0620143J | 6 A | Class I- Divisions 1 & 2- Groups C & D / Class I- Zones 1 & 2 Groups IIB / Ignition Temperature Code T3A- 356° F | Not Required | 0' - 8" | 60 Hz | 1' - 4" | 2' - 2" | 1 | 1 | No | Yes | No | No | 27 lbs | S1 | 4776.0 Btu/h | 2 | 240 V | 1400 W |
| QX-254-F0620143N | 5 A | Class I- Divisions 1 & 2- Groups C & D / Class I- Zones 1 & 2 Groups IIB / Ignition Temperature Code T3A- 356° F | Not Required | 0' - 8" | 60 Hz | 1' - 4" | 2' - 2" | 1 | 1 | No | Yes | No | No | 27 lbs | S1 | 4776.0 Btu/h | 2 | 277 V | 1400 W |
| QX-254-F0620143I | 4 A | Class I- Divisions 1 & 2- Groups C & D / Class I- Zones 1 & 2 Groups IIB / Ignition Temperature Code T3A- 356° F | B2 | 0' - 8" | 60 Hz | 1' - 4" | 2' - 2" | 1 | 1 | No | Yes | No | No | 27 lbs | B2S1 | 4776.0 Btu/h | 2 | 347 V | 1400 W |
| QX-254-F0630233B | 19 A | Class I- Divisions 1 & 2- Groups C & D / Class I- Zones 1 & 2 Groups IIB / Ignition Temperature Code T3A- 356° F | Not Required | 0' - 8" | 60 Hz | 1' - 4" | 3' - 3" | 1 | 1 | No | No | Yes | No | 36 lbs | S1 | 7847.0 Btu/h | 3 | 120 V | 2300 W |
| QX-254-F0630233C | 11 A | Class I- Divisions 1 & 2- Groups C & D / Class I- Zones 1 & 2 Groups IIB / Ignition Temperature Code T3A- 356° F | Not Required | 0' - 8" | 60 Hz | 1' - 4" | 3' - 3" | 1 | 1 | No | No | Yes | No | 36 lbs | S1 | 7847.0 Btu/h | 3 | 208 V | 2300 W |
| QX-254-F0630233D | 6 A | Class I- Divisions 1 & 2- Groups C & D / Class I- Zones 1 & 2 Groups IIB / Ignition Temperature Code T3A- 356° F | B2 | 0' - 8" | 60 Hz | 1' - 4" | 3' - 3" | 3 | 1 | No | No | Yes | No | 36 lbs | B2S1 | 7847.0 Btu/h | 3 | 208 V | 2300 W |
| QX-254-F0630233J | 10 A | Class I- Divisions 1 & 2- Groups C & D / Class I- Zones 1 & 2 Groups IIB / Ignition Temperature Code T3A- 356° F | Not Required | 0' - 8" | 60 Hz | 1' - 4" | 3' - 3" | 1 | 1 | No | No | Yes | No | 36 lbs | S1 | 7847.0 Btu/h | 3 | 240 V | 2300 W |
| QX-254-F0630233N | 8 A | Class I- Divisions 1 & 2- Groups C & D / Class I- Zones 1 & 2 Groups IIB / Ignition Temperature Code T3A- 356° F | Not Required | 0' - 8" | 60 Hz | 1' - 4" | 3' - 3" | 1 | 1 | No | No | Yes | No | 36 lbs | S1 | 7847.0 Btu/h | 3 | 277 V | 2300 W |
| QX-254-F0630233I | 7 A | Class I- Divisions 1 & 2- Groups C & D / Class I- Zones 1 & 2 Groups IIB / Ignition Temperature Code T3A- 356° F | B2 | 0' - 8" | 60 Hz | 1' - 4" | 3' - 3" | 1 | 1 | No | No | Yes | No | 36 lbs | B2S1 | 7847.0 Btu/h | 3 | 347 V | 2300 W |
| QX-254-F0630233U | 3 A | Class I- Divisions 1 & 2- Groups C & D / Class I- Zones 1 & 2 Groups IIB / Ignition Temperature Code T3A- 356° F | B2 | 0' - 8" | 60 Hz | 1' - 4" | 3' - 3" | 3 | 1 | No | No | Yes | No | 36 lbs | B2S1 | 7847.0 Btu/h | 3 | 480 V | 2300 W |
| QX-254-F0630233Z | 2 A | Class I- Divisions 1 & 2- Groups C & D / Class I- Zones 1 & 2 Groups IIB / Ignition Temperature Code T3A- 356° F | B2 | 0' - 8" | 60 Hz | 1' - 4" | 3' - 3" | 3 | 1 | No | No | Yes | No | 36 lbs | B2S1 | 7847.0 Btu/h | 3 | 600 V | 2300 W |
| QX-254-F0640323C | 15 A | Class I- Divisions 1 & 2- Groups C & D / Class I- Zones 1 & 2 Groups IIB / Ignition Temperature Code T3A- 356° F | Not Required | 0' - 8" | 60 Hz | 1' - 4" | 5' - 7 1/2" | 1 | 1 | No | No | No | Yes | 60 lbs | S1 | 10918.0 Btu/h | 4 | 208 V | 3200 W |
| QX-254-F0640323D | 9 A | Class I- Divisions 1 & 2- Groups C & D / Class I- Zones 1 & 2 Groups IIB / Ignition Temperature Code T3A- 356° F | B2 | 0' - 8" | 60 Hz | 1' - 4" | 5' - 7 1/2" | 3 | 1 | No | No | No | Yes | 60 lbs | B2S1 | 10918.0 Btu/h | 4 | 208 V | 3200 W |
| QX-254-F0640323J | 13 A | Class I- Divisions 1 & 2- Groups C & D / Class I- Zones 1 & 2 Groups IIB / Ignition Temperature Code T3A- 356° F | Not Required | 0' - 8" | 60 Hz | 1' - 4" | 5' - 7 1/2" | 1 | 1 | No | No | No | Yes | 60 lbs | S1 | 10918.0 Btu/h | 4 | 240 V | 3200 W |
| QX-254-F0640323N | 12 A | Class I- Divisions 1 & 2- Groups C & D / Class I- Zones 1 & 2 Groups IIB / Ignition Temperature Code T3A- 356° F | Not Required | 0' - 8" | 60 Hz | 1' - 4" | 5' - 7 1/2" | 1 | 1 | No | No | No | Yes | 60 lbs | S1 | 10918.0 Btu/h | 4 | 277 V | 3200 W |
| QX-254-F0640323I | 9 A | Class I- Divisions 1 & 2- Groups C & D / Class I- Zones 1 & 2 Groups IIB / Ignition Temperature Code T3A- 356° F | B2 | 0' - 8" | 60 Hz | 1' - 4" | 5' - 7 1/2" | 1 | 1 | No | No | No | Yes | 60 lbs | B2S1 | 10918.0 Btu/h | 4 | 347 V | 3200 W |
| QX-254-F0640323U | 4 A | Class I- Divisions 1 & 2- Groups C & D / Class I- Zones 1 & 2 Groups IIB / Ignition Temperature Code T3A- 356° F | B2 | 0' - 8" | 60 Hz | 1' - 4" | 5' - 7 1/2" | 3 | 1 | No | No | No | Yes | 60 lbs | B2S1 | 10918.0 Btu/h | 4 | 480 V | 3200 W |
| QX-254-F0640323Z | 3 A | Class I- Divisions 1 & 2- Groups C & D / Class I- Zones 1 & 2 Groups IIB / Ignition Temperature Code T3A- 356° F | B2 | 0' - 8" | 60 Hz | 1' - 4" | 5' - 7 1/2" | 3 | 1 | No | No | No | Yes | 60 lbs | B2S1 | 10918.0 Btu/h | 4 | 600 V | 3200 W |
| QX-254-F0640503D | 14 A | Class I- Divisions 1 & 2- Groups C & D / Class I- Zones 1 & 2 Groups IIB / Ignition Temperature Code T3A- 356° F | B2 | 0' - 8" | 60 Hz | 1' - 4" | 5' - 7 1/2" | 3 | 1 | No | No | No | Yes | 60 lbs | B2S1 | 17060.0 Btu/h | 4 | 208 V | 5000 W |
| QX-254-F0640503J | 21 A | Class I- Divisions 1 & 2- Groups C & D / Class I- Zones 1 & 2 Groups IIB / Ignition Temperature Code T3A- 356° F | Not Required | 0' - 8" | 60 Hz | 1' - 4" | 5' - 7 1/2" | 1 | 1 | No | No | No | Yes | 60 lbs | S1 | 17060.0 Btu/h | 4 | 240 V | 5000 W |
| QX-254-F0640503N | 18 A | Class I- Divisions 1 & 2- Groups C & D / Class I- Zones 1 & 2 Groups IIB / Ignition Temperature Code T3A- 356° F | Not Required | 0' - 8" | 60 Hz | 1' - 4" | 5' - 7 1/2" | 1 | 1 | No | No | No | Yes | 60 lbs | S1 | 17060.0 Btu/h | 4 | 277 V | 5000 W |
| QX-254-F0640503I | 14 A | Class I- Divisions 1 & 2- Groups C & D / Class I- Zones 1 & 2 Groups IIB / Ignition Temperature Code T3A- 356° F | B2 | 0' - 8" | 60 Hz | 1' - 4" | 5' - 7 1/2" | 1 | 1 | No | No | No | Yes | 60 lbs | B2S1 | 17060.0 Btu/h | 4 | 347 V | 5000 W |
| QX-254-F0640503U | 6 A | Class I- Divisions 1 & 2- Groups C & D / Class I- Zones 1 & 2 Groups IIB / Ignition Temperature Code T3A- 356° F | B2 | 0' - 8" | 60 Hz | 1' - 4" | 5' - 7 1/2" | 3 | 1 | No | No | No | Yes | 60 lbs | B2S1 | 17060.0 Btu/h | 4 | 480 V | 5000 W |
| QX-254-F0640503Z | 5 A | Class I- Divisions 1 & 2- Groups C & D / Class I- Zones 1 & 2 Groups IIB / Ignition Temperature Code T3A- 356° F | B2 | 0' - 8" | 60 Hz | 1' - 4" | 5' - 7 1/2" | 3 | 1 | No | No | No | Yes | 60 lbs | B2S1 | 17060.0 Btu/h | 4 | 600 V | 5000 W |
| QX-254-F0810054B | 4 A | Class I- Divisions 1 & 2- Groups B- C & D / Class II- Divisions 1 & 2- Groups E- F & G / Ignition Temperature Code T3C- 320° F |  | 0' - 4 1/2" | 60 Hz | 0' - 6" | 2' - 2" | 1 | 1 | Yes | No | No | No | 13 lbs | 1007002 | 1706.0 Btu/h | 1 | 120 V | 500 W |
| QX-254-F0810054C | 2 A | Class I- Divisions 1 & 2- Groups B- C & D / Class II- Divisions 1 & 2- Groups E- F & G / Ignition Temperature Code T3C- 320° F |  | 0' - 4 1/2" | 60 Hz | 0' - 6" | 2' - 2" | 1 | 1 | Yes | No | No | No | 13 lbs | 1007002 | 1706.0 Btu/h | 1 | 208 V | 500 W |
| QX-254-F0810054J | 2 A | Class I- Divisions 1 & 2- Groups B- C & D / Class II- Divisions 1 & 2- Groups E- F & G / Ignition Temperature Code T3C- 320° F |  | 0' - 4 1/2" | 60 Hz | 0' - 6" | 2' - 2" | 1 | 1 | Yes | No | No | No | 13 lbs | 1007002 | 1706.0 Btu/h | 1 | 240 V | 500 W |
| QX-254-F0810054N | 2 A | Class I- Divisions 1 & 2- Groups B- C & D / Class II- Divisions 1 & 2- Groups E- F & G / Ignition Temperature Code T3C- 320° F |  | 0' - 4 1/2" | 60 Hz | 0' - 6" | 2' - 2" | 1 | 1 | Yes | No | No | No | 13 lbs | 1007002 | 1706.0 Btu/h | 1 | 277 V | 500 W |
| QX-254-F0820104B | 8 A | Class I- Divisions 1 & 2- Groups B- C & D / Class II- Divisions 1 & 2- Groups E- F & G / Ignition Temperature Code T3C- 320° F | Not Required | 0' - 8" | 60 Hz | 1' - 4" | 2' - 2" | 1 | 1 | No | Yes | No | No | 27 lbs | S1 | 3412.0 Btu/h | 2 | 120 V | 1000 W |
| QX-254-F0820104C | 5 A | Class I- Divisions 1 & 2- Groups B- C & D / Class II- Divisions 1 & 2- Groups E- F & G / Ignition Temperature Code T3C- 320° F | Not Required | 0' - 8" | 60 Hz | 1' - 4" | 2' - 2" | 1 | 1 | No | Yes | No | No | 27 lbs | S1 | 3412.0 Btu/h | 2 | 208 V | 1000 W |
| QX-254-F0820104J | 4 A | Class I- Divisions 1 & 2- Groups B- C & D / Class II- Divisions 1 & 2- Groups E- F & G / Ignition Temperature Code T3C- 320° F | Not Required | 0' - 8" | 60 Hz | 1' - 4" | 2' - 2" | 1 | 1 | No | Yes | No | No | 27 lbs | S1 | 3412.0 Btu/h | 2 | 240 V | 1000 W |
| QX-254-F0820104N | 4 A | Class I- Divisions 1 & 2- Groups B- C & D / Class II- Divisions 1 & 2- Groups E- F & G / Ignition Temperature Code T3C- 320° F | Not Required | 0' - 8" | 60 Hz | 1' - 4" | 2' - 2" | 1 | 1 | No | Yes | No | No | 27 lbs | S1 | 3412.0 Btu/h | 2 | 277 V | 1000 W |
| QX-254-F0820104I | 3 A | Class I- Divisions 1 & 2- Groups B- C & D / Class II- Divisions 1 & 2- Groups E- F & G / Ignition Temperature Code T3C- 320° F | B2 | 0' - 8" | 60 Hz | 1' - 4" | 2' - 2" | 1 | 1 | No | Yes | No | No | 27 lbs | B2S1 | 3412.0 Btu/h | 2 | 347 V | 1000 W |
| QX-254-F0830174B | 14 A | Class I- Divisions 1 & 2- Groups B- C & D / Class II- Divisions 1 & 2- Groups E- F & G / Ignition Temperature Code T3C- 320° F | Not Required | 0' - 8" | 60 Hz | 1' - 4" | 3' - 3" | 1 | 1 | No | No | Yes | No | 36 lbs | S1 | 5800.0 Btu/h | 3 | 120 V | 1700 W |
| QX-254-F0830174C | 8 A | Class I- Divisions 1 & 2- Groups B- C & D / Class II- Divisions 1 & 2- Groups E- F & G / Ignition Temperature Code T3C- 320° F | Not Required | 0' - 8" | 60 Hz | 1' - 4" | 3' - 3" | 1 | 1 | No | No | Yes | No | 36 lbs | S1 | 5800.0 Btu/h | 3 | 208 V | 1700 W |
| QX-254-F0830174D | 5 A | Class I- Divisions 1 & 2- Groups B- C & D / Class II- Divisions 1 & 2- Groups E- F & G / Ignition Temperature Code T3C- 320° F | B2 | 0' - 8" | 60 Hz | 1' - 4" | 3' - 3" | 3 | 1 | No | No | Yes | No | 36 lbs | B2S1 | 5800.0 Btu/h | 3 | 208 V | 1700 W |
| QX-254-F0830174J | 7 A | Class I- Divisions 1 & 2- Groups B- C & D / Class II- Divisions 1 & 2- Groups E- F & G / Ignition Temperature Code T3C- 320° F | Not Required | 0' - 8" | 60 Hz | 1' - 4" | 3' - 3" | 1 | 1 | No | No | Yes | No | 36 lbs | S1 | 5800.0 Btu/h | 3 | 240 V | 1700 W |
| QX-254-F0830174N | 6 A | Class I- Divisions 1 & 2- Groups B- C & D / Class II- Divisions 1 & 2- Groups E- F & G / Ignition Temperature Code T3C- 320° F | Not Required | 0' - 8" | 60 Hz | 1' - 4" | 3' - 3" | 1 | 1 | No | No | Yes | No | 36 lbs | S1 | 5800.0 Btu/h | 3 | 277 V | 1700 W |
| QX-254-F0830174I | 5 A | Class I- Divisions 1 & 2- Groups B- C & D / Class II- Divisions 1 & 2- Groups E- F & G / Ignition Temperature Code T3C- 320° F | B2 | 0' - 8" | 60 Hz | 1' - 4" | 3' - 3" | 1 | 1 | No | No | Yes | No | 36 lbs | B2S1 | 5800.0 Btu/h | 3 | 347 V | 1700 W |
| QX-254-F0830174U | 2 A | Class I- Divisions 1 & 2- Groups B- C & D / Class II- Divisions 1 & 2- Groups E- F & G / Ignition Temperature Code T3C- 320° F | B2 | 0' - 8" | 60 Hz | 1' - 4" | 3' - 3" | 3 | 1 | No | No | Yes | No | 36 lbs | B2S1 | 5800.0 Btu/h | 3 | 480 V | 1700 W |
| QX-254-F0830174Z | 2 A | Class I- Divisions 1 & 2- Groups B- C & D / Class II- Divisions 1 & 2- Groups E- F & G / Ignition Temperature Code T3C- 320° F | B2 | 0' - 8" | 60 Hz | 1' - 4" | 3' - 3" | 3 | 1 | No | No | Yes | No | 36 lbs | B2S1 | 5800.0 Btu/h | 3 | 600 V | 1700 W |
| QX-254-F0840324C | 15 A | Class I- Divisions 1 & 2- Groups B- C & D / Class II- Divisions 1 & 2- Groups E- F & G / Ignition Temperature Code T3C- 320° F | Not Required | 0' - 8" | 60 Hz | 1' - 4" | 5' - 7 1/2" | 1 | 1 | No | No | No | Yes | 36 lbs | S1 | 10918.0 Btu/h | 4 | 208 V | 3200 W |
| QX-254-F0840324D | 9 A | Class I- Divisions 1 & 2- Groups B- C & D / Class II- Divisions 1 & 2- Groups E- F & G / Ignition Temperature Code T3C- 320° F | B2 | 0' - 8" | 60 Hz | 1' - 4" | 5' - 7 1/2" | 3 | 1 | No | No | No | Yes | 60 lbs | B2S1 | 10918.0 Btu/h | 4 | 208 V | 3200 W |
| QX-254-F0840324J | 13 A | Class I- Divisions 1 & 2- Groups B- C & D / Class II- Divisions 1 & 2- Groups E- F & G / Ignition Temperature Code T3C- 320° F | Not Required | 0' - 8" | 60 Hz | 1' - 4" | 5' - 7 1/2" | 1 | 1 | No | No | No | Yes | 60 lbs | S1 | 10918.0 Btu/h | 4 | 240 V | 3200 W |
| QX-254-F0840324N | 12 A | Class I- Divisions 1 & 2- Groups B- C & D / Class II- Divisions 1 & 2- Groups E- F & G / Ignition Temperature Code T3C- 320° F | Not Required | 0' - 8" | 60 Hz | 1' - 4" | 5' - 7 1/2" | 1 | 1 | No | No | No | Yes | 60 lbs | S1 | 10918.0 Btu/h | 4 | 277 V | 3200 W |
| QX-254-F0840324I | 9 A | Class I- Divisions 1 & 2- Groups B- C & D / Class II- Divisions 1 & 2- Groups E- F & G / Ignition Temperature Code T3C- 320° F | B2 | 0' - 8" | 60 Hz | 1' - 4" | 5' - 7 1/2" | 1 | 1 | No | No | No | Yes | 60 lbs | B2S1 | 10918.0 Btu/h | 4 | 347 V | 3200 W |
| QX-254-F0840324U | 4 A | Class I- Divisions 1 & 2- Groups B- C & D / Class II- Divisions 1 & 2- Groups E- F & G / Ignition Temperature Code T3C- 320° F | B2 | 0' - 8" | 60 Hz | 1' - 4" | 5' - 7 1/2" | 3 | 1 | No | No | No | Yes | 60 lbs | B2S1 | 10918.0 Btu/h | 4 | 480 V | 3200 W |
| QX-254-F0840324Z | 3 A | Class I- Divisions 1 & 2- Groups B- C & D / Class II- Divisions 1 & 2- Groups E- F & G / Ignition Temperature Code T3C- 320° F | B2 | 0' - 8" | 60 Hz | 1' - 4" | 5' - 7 1/2" | 3 | 1 | No | No | No | Yes | 60 lbs | B2S1 | 10918.0 Btu/h | 4 | 600 V | 3200 W |

note: column(s) folded — value = type name in every type: Model

## geometry (parser evidence)
native form markers: Sweep x17
no freeform markers — native parametric forms only
